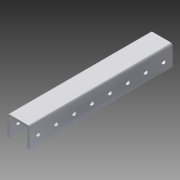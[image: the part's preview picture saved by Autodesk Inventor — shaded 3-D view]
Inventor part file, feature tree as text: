
AUTODESK INVENTOR PART (.ipt)
format: ipt  version: 2015 (Build 190159000, 159)  size: 187,904 bytes
history: native  units: in
note: dims shown in document units (in); Inventor stores cm internally (conversion verified against a paired STEP export)
features: extrude x2, sketch x2, pattern_linear x1
ambient origin geometry x8: Origin, YZ Plane, XZ Plane, XY Plane, X Axis, Y Axis, Z Axis, Center Point
bodies: Solid1 (feature_tree)
feature tree (5):
  extrude  "Extrusion1"  Depth=8.0in
  extrude  "Extrusion4"  Depth=0.5in
  pattern_linear  "Rectangular Pattern3"  Spacing1=0.5in  [1 undecoded]
  sketch  "Sketch1"  dims[d0=1.13in d1=1.25in d2=0.125in d3=0.125in d4=0.125in d5=8.0in]
  sketch  "Sketch4"  dims[d6=0.0in d34=0.5in d35=0.5in d36=0.25in d37=1.0in d38=0.0in d39=5.9055in d41=1.0in d42=5.9055in d44=1.0in]
note: 1 required parameter value undecoded (feature->parameter linkage not recoverable at this tier; creation-order binding heuristic only, values carry confidence <= 0.55)
